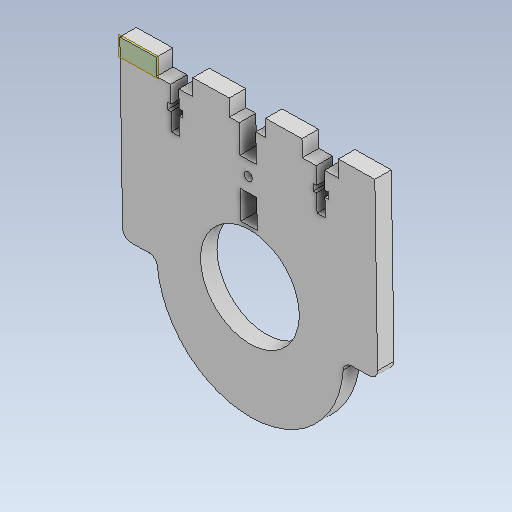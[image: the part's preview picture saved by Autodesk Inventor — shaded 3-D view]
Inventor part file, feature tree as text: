
AUTODESK INVENTOR PART (.ipt)
format: ipt  version: 2021.1 (Build 251245010, 245A)  size: 213,504 bytes
history: native  units: mm
features: reference x25, other x7, extrude x2, sketch x2
ambient origin geometry x8: Origin, YZ Plane, XZ Plane, XY Plane, X Axis, Y Axis, Z Axis, Center Point
bodies: Body1 (feature_tree)
feature tree (36):
  other  "Твердое тело1"
  other  "РабПлоскость1"
  extrude  "Выдавливание1"  Depth=6.0mm
  extrude  "Выдавливание2"  Depth=6.0mm
  sketch  "Эскиз1"
  reference  "Ссылка1"
  reference  "Ссылка2"
  reference  "Ссылка3"
  reference  "Ссылка4"
  reference  "Ссылка5"
  reference  "Ссылка6"
  reference  "Ссылка9"
  reference  "Ссылка10"
  reference  "Ссылка13"
  reference  "Ссылка14"
  reference  "Ссылка17"
  reference  "Ссылка18"
  reference  "Ссылка19"
  reference  "Ссылка20"
  reference  "Ссылка21"
  reference  "Ссылка22"
  sketch  "Эскиз2"
  reference  "Ссылка36"
  reference  "Ссылка60"
  reference  "Ссылка61"
  reference  "Ссылка62"
  reference  "Ссылка63"
  reference  "Ссылка65"
  reference  "Ссылка67"
  reference  "Ссылка68"
  reference  "Ссылка70"
  other  "<userpath>\Documents\Savka\3d\Korp.iam"
  other  "Korp.iam"
  other  "Korpus 5:1"
  other  "Korpus 3:1"
  other  "44260_txm torquenado dc motor:1"
